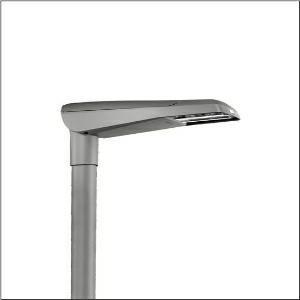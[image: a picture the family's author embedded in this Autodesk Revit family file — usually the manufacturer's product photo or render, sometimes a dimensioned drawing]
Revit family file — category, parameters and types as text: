
# Revit family: streetlight_sl_11_iq_micro___p1_0a_5xc1cc1f08de_50c8
name_source: partatom
category: Lighting Fixtures
units: mm (PartAtom-declared; Revit-internal decimal feet)

## family parameters
Cut with Voids When Loaded = No
Host = Face
Light Source = No
Part Type = Normal
Room Calculation Point = No
Round Connector Dimension = Use Diameter
Shared = No

## types (1)
- --- (1 x LED, 2620 lm, 24.2 W, 2200K)
    Apparent Load = 24 VA
    CIE Flux Codes = 29 63 93 100 100
    Color Rendering = 70
    Color Temperature = 2200K
    Default Elevation = 1800 mm
    Description = Streetlight SL 11 iQ micro, mast luminaire, primary light control with 3 zone facetted reflector, of plastic, silver coated, highly specular, primary optical cover: cover, of PMMA, transparent, light distribution: P1.0a, light emission: direct distribution, primary light characteristic: asymmetric, installation type: post-top, side-entry, lamps: LED, High Power LED, rated values: 3.150lm | 24,1W | 130,7lm/W (begin service life); end service life: 3.150lm | 24,6W; at 50% lumin. flux: 1.575lm | 11,9W | 132,4lm/W, colour temperature: 2200/2700/3000/4000K, colour rendering: CRI > 70, light colour: 722/727/730/740, light setting 1 begin service life: 100% | 3.150lm | 24,1W | 130,7lm/W | 3.000K, light setting 1 end service life: 24,6W, further light settings possible, control: Street-Remote, Auto-Match, Temp-Guard, Lumen-Switch, Night-Set, Smart-Wire, Light-Fading, Desk-Remote (wireless, voltage-free reading and setting of iQ features in the workshop via application-optimized NFC function/RFID function), optimised constant luminous flux control (CLO 2.0), with cable H07RN-F 5x 1.5mm², mains connection: 220..240V, AC, 50/60Hz, connection cable pre-assembled, cable length: 6,5m, luminaire housing, of diecast aluminium, powder-coated, Siteco® metallic grey (DB 702S), please order mast flange separately, inclination adjustable without tools: 0°, 5°, 10°, 15° (post-top) | 0°, -5°, -10°, -15° (side-entry), sealing non-destructively replaceable, multi-level sealing system, length: 600mm, width: 174mm, height: 116mm, mast flange for spigot size: 42mm (side-entry): 5XC10008XM4, 60/48mm (side-entry/post-top): 5XC10108XM2, 76/60mm (side-entry/post-top): 5XC10108XM1, equipment: Power, protection rating (complete): IP66, insulation class (complete): insulation class II (safety insulation), certification: CE, ENEC, ENEC+, VDE, impact resistance: IK10, permissible operating ambient temperature for outdoor applications: -25..+50°C, standard-compliant lighting for roads and squares, Environmental Product Declaration (EPD) tested and certified by an independent institute, packaging unit: 1 piece

Light Distribution: P1.0a
    Height = 116 mm
    Lamp = 1 x LED
    Lamp Light Flux = 2620 lm
    Lamp Power = 24.2 W
    Lamp count = 1
    Length = 600 mm
    Luminous efficacy = 108 lm/W
    Manufacturer = Siteco
    ModVariant = No
    Model = 5XC1CC1F08DE
    Number of Poles = 1
    OnlyDefault = Yes
    Power Factor = 1
    Product Name = Streetlight SL 11 iQ micro | P1.0a
    Product group = mast luminaire | pylon top
    ProductGroupID = 6100
    Protection Class = Protection class II
    Protection Degree = IP 66
    RLX_Detail_Level = 1
    RLX_Emergency_Light_Flux = 0 lm
    RLX_Emergency_Type = 0
    RLX_Emergency_Type_DB = No
    RlxData = <blob elided: 59197 chars, md5=49a889cc>
    Socket = socket
    Standby Power = 0 W
    System Light Flux = 2620 lm
    System Power = 24 W
    Type Comments = individual setting: luminous flux: 100 % | dim-lin: 254 | 644 mA
    Type Image = l_1006566.jpg
    URL = http://relux.com
    VarID = @adj_057843
    Voltage = 0 V
    Weight = 0.00 kg
    Width = 174 mm

## geometry (parser evidence)
native form markers: Blend x4, Sweep x11
no freeform markers — native parametric forms only
